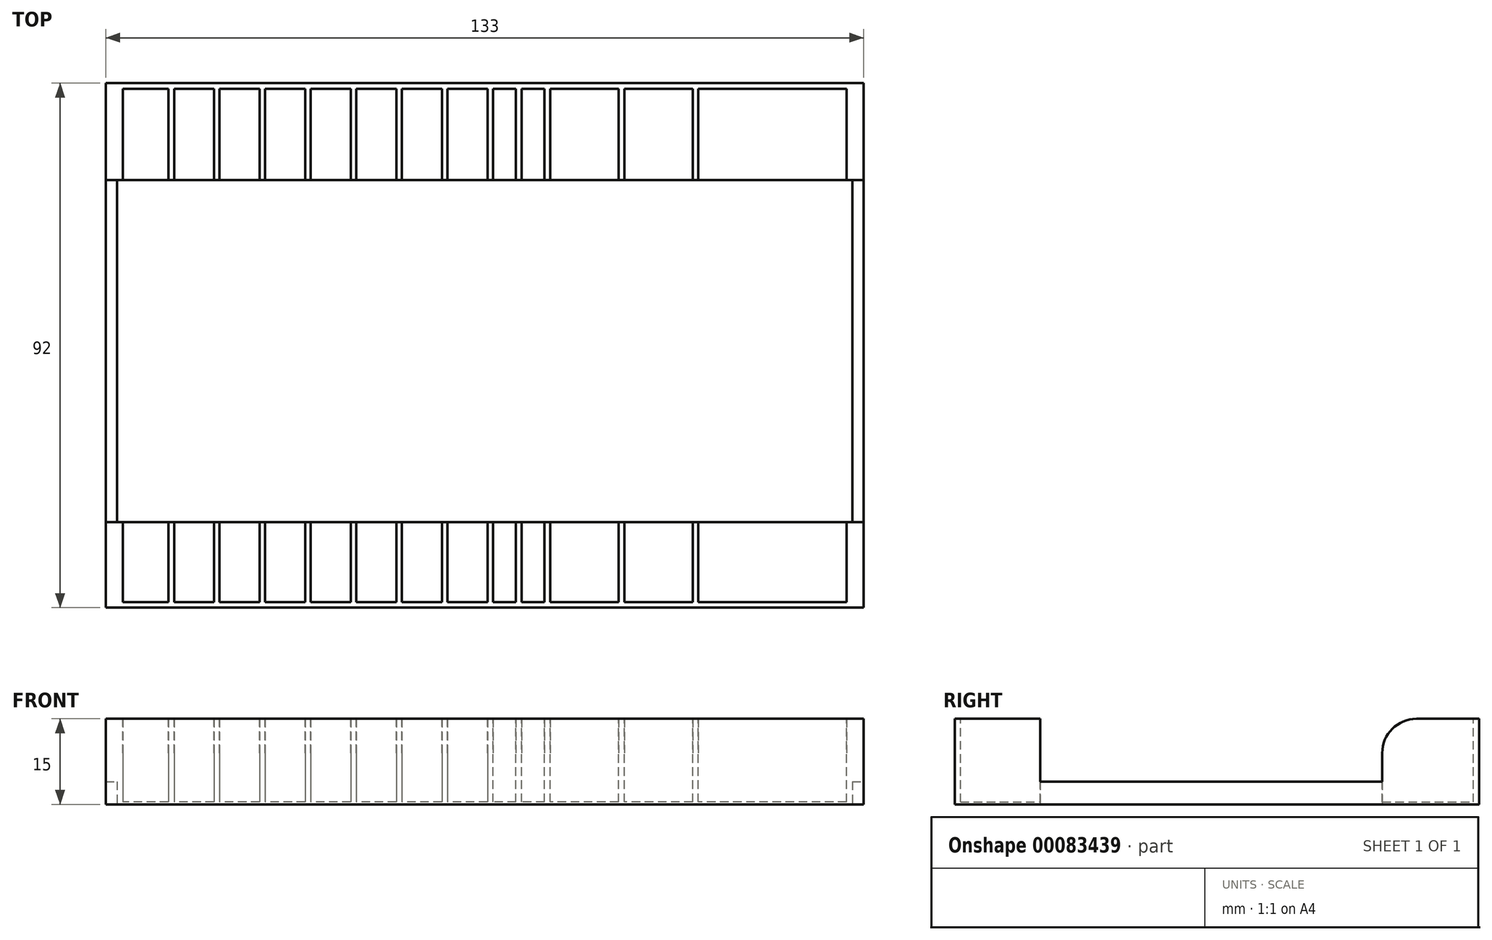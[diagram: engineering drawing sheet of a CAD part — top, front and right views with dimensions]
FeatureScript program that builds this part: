
annotation { "Feature Type Name" : "Feature", "Feature Type Description" : "" }
export const myFeature = defineFeature(function(context is Context, id is Id, definition is map)
    precondition{}
    {
        {
            assignVariable(context, id + "F0", {"name" : "holderHeight", "anyValue" : 15});
        }
        {
            var Q0;
            Q0=qCreatedBy(makeId("Top.planeOp"),FACE);
            var sketch = newSketch(context, id + "F1", { "sketchPlane" : qUnion([Q0])});
            skLineSegment(sketch, "E0.bottom", {"start": v(-58, -45) * mm, "end": v(71, -45) * mm});
            skLineSegment(sketch, "E0.top", {"start": v(-58, 47) * mm, "end": v(71, 47) * mm});
            skLineSegment(sketch, "E0.left", {"start": v(-58, -45) * mm, "end": v(-58, 47) * mm});
            skLineSegment(sketch, "E0.right", {"start": v(71, -45) * mm, "end": v(71, 47) * mm});
            skSolve(sketch);
        }
        {
            var Q0;
            Q0=makeQuery(id+"F1.imprint","IMPRINT",FACE,{"disambiguationData":[TD([[makeQuery(id+"F1.imprint","IMPRINT",EDGE,{"derivedFrom":sQuery(id+"F1.wireOp",EDGE,"E0.bottom")}),1.0]])]});
            extrude(context, id + "F2", {"entities" : qUnion([Q0]), "depth" : getVariable(context, 'holderHeight') * mm});
        }
        {
            var Q0;
            Q0=makeQuery(id+"F2.opExtrude","CAP_FACE",FACE,{"disambiguationData":[OSD([sQuery(id+"F1.wireOp",EDGE,"E0.bottom"),sQuery(id+"F1.wireOp",EDGE,"E0.top"),sQuery(id+"F1.wireOp",EDGE,"E0.left"),sQuery(id+"F1.wireOp",EDGE,"E0.right")])],"isStart":false});
            var sketch = newSketch(context, id + "F3", { "sketchPlane" : qUnion([Q0])});
            skPoint(sketch, "E1.middle", {"position": v(0, 1) * mm});
            skLineSegment(sketch, "E2.bottom", {"start": v(-49, 46) * mm, "end": v(-57, 46) * mm});
            skLineSegment(sketch, "E2.top", {"start": v(-49, -44) * mm, "end": v(-57, -44) * mm});
            skLineSegment(sketch, "E2.left", {"start": v(-49, 46) * mm, "end": v(-49, -44) * mm});
            skLineSegment(sketch, "E2.right", {"start": v(-57, 46) * mm, "end": v(-57, -44) * mm});
            skPoint(sketch, "E2.middle", {"position": v(-53, 1) * mm});
            skLineSegment(sketch, "E3", {"start": v(0, 1) * mm, "end": v(-109.38, 1) * mm, "construction": true});
            skLineSegment(sketch, "E4.bottom", {"start": v(-41, 46) * mm, "end": v(-48, 46) * mm});
            skLineSegment(sketch, "E4.top", {"start": v(-41, -44) * mm, "end": v(-48, -44) * mm});
            skLineSegment(sketch, "E4.left", {"start": v(-41, 46) * mm, "end": v(-41, -44) * mm});
            skLineSegment(sketch, "E4.right", {"start": v(-48, 46) * mm, "end": v(-48, -44) * mm});
            skPoint(sketch, "E4.middle", {"position": v(-44.5, 1) * mm});
            skPoint(sketch, "E4.cornerSnap0", {"position": v(-53, 46) * mm});
            skLineSegment(sketch, "E5.1.0.0", {"start": v(-33, 46) * mm, "end": v(-33, -44) * mm});
            skLineSegment(sketch, "E5.1.0.1", {"start": v(-33, 46) * mm, "end": v(-40, 46) * mm});
            skLineSegment(sketch, "E5.1.0.2", {"start": v(-40, 46) * mm, "end": v(-40, -44) * mm});
            skLineSegment(sketch, "E5.1.0.3", {"start": v(-33, -44) * mm, "end": v(-40, -44) * mm});
            skLineSegment(sketch, "E5.2.0.0", {"start": v(-25, 46) * mm, "end": v(-25, -44) * mm});
            skLineSegment(sketch, "E5.2.0.1", {"start": v(-25, 46) * mm, "end": v(-32, 46) * mm});
            skLineSegment(sketch, "E5.2.0.2", {"start": v(-32, 46) * mm, "end": v(-32, -44) * mm});
            skLineSegment(sketch, "E5.2.0.3", {"start": v(-25, -44) * mm, "end": v(-32, -44) * mm});
            skLineSegment(sketch, "E5.3.0.0", {"start": v(-17, 46) * mm, "end": v(-17, -44) * mm});
            skLineSegment(sketch, "E5.3.0.1", {"start": v(-17, 46) * mm, "end": v(-24, 46) * mm});
            skLineSegment(sketch, "E5.3.0.2", {"start": v(-24, 46) * mm, "end": v(-24, -44) * mm});
            skLineSegment(sketch, "E5.3.0.3", {"start": v(-17, -44) * mm, "end": v(-24, -44) * mm});
            skLineSegment(sketch, "E5.4.0.0", {"start": v(-9, 46) * mm, "end": v(-9, -44) * mm});
            skLineSegment(sketch, "E5.4.0.1", {"start": v(-9, 46) * mm, "end": v(-16, 46) * mm});
            skLineSegment(sketch, "E5.4.0.2", {"start": v(-16, 46) * mm, "end": v(-16, -44) * mm});
            skLineSegment(sketch, "E5.4.0.3", {"start": v(-9, -44) * mm, "end": v(-16, -44) * mm});
            skLineSegment(sketch, "E5.5.0.0", {"start": v(-1, 46) * mm, "end": v(-1, -44) * mm});
            skLineSegment(sketch, "E5.5.0.1", {"start": v(-1, 46) * mm, "end": v(-8, 46) * mm});
            skLineSegment(sketch, "E5.5.0.2", {"start": v(-8, 46) * mm, "end": v(-8, -44) * mm});
            skLineSegment(sketch, "E5.5.0.3", {"start": v(-1, -44) * mm, "end": v(-8, -44) * mm});
            skLineSegment(sketch, "E5.direction1", {"start": v(-41, -44) * mm, "end": v(-33, -44) * mm, "construction": true});
            skLineSegment(sketch, "E6.0.6.0", {"start": v(7, 46) * mm, "end": v(7, -44) * mm});
            skLineSegment(sketch, "E6.3.6.0", {"start": v(7, 46) * mm, "end": v(0, 46) * mm});
            skLineSegment(sketch, "E6.6.6.0", {"start": v(0, 46) * mm, "end": v(0, -44) * mm});
            skLineSegment(sketch, "E6.9.6.0", {"start": v(7, -44) * mm, "end": v(0, -44) * mm});
            skLineSegment(sketch, "E7", {"start": v(0, 1) * mm, "end": v(83.05, 1) * mm, "construction": true});
            skLineSegment(sketch, "E8.bottom", {"start": v(8, -44) * mm, "end": v(12, -44) * mm});
            skLineSegment(sketch, "E8.top", {"start": v(8, 46) * mm, "end": v(12, 46) * mm});
            skLineSegment(sketch, "E8.left", {"start": v(8, -44) * mm, "end": v(8, 46) * mm});
            skLineSegment(sketch, "E8.right", {"start": v(12, -44) * mm, "end": v(12, 46) * mm});
            skPoint(sketch, "E8.middle", {"position": v(10, 1) * mm});
            skLineSegment(sketch, "E9.bottom", {"start": v(13, -44) * mm, "end": v(17, -44) * mm});
            skLineSegment(sketch, "E9.top", {"start": v(13, 46) * mm, "end": v(17, 46) * mm});
            skLineSegment(sketch, "E9.left", {"start": v(13, -44) * mm, "end": v(13, 46) * mm});
            skLineSegment(sketch, "E9.right", {"start": v(17, -44) * mm, "end": v(17, 46) * mm});
            skPoint(sketch, "E9.middle", {"position": v(15, 1) * mm});
            skLineSegment(sketch, "E10.bottom", {"start": v(18, -44) * mm, "end": v(30, -44) * mm});
            skLineSegment(sketch, "E10.top", {"start": v(18, 46) * mm, "end": v(30, 46) * mm});
            skLineSegment(sketch, "E10.left", {"start": v(18, -44) * mm, "end": v(18, 46) * mm});
            skLineSegment(sketch, "E10.right", {"start": v(30, -44) * mm, "end": v(30, 46) * mm});
            skPoint(sketch, "E10.middle", {"position": v(24, 1) * mm});
            skLineSegment(sketch, "E11.1.0.0", {"start": v(43, -44) * mm, "end": v(43, 46) * mm});
            skLineSegment(sketch, "E11.1.0.1", {"start": v(31, 46) * mm, "end": v(43, 46) * mm});
            skLineSegment(sketch, "E11.1.0.2", {"start": v(31, -44) * mm, "end": v(31, 46) * mm});
            skLineSegment(sketch, "E11.1.0.3", {"start": v(31, -44) * mm, "end": v(43, -44) * mm});
            skLineSegment(sketch, "E11.direction1", {"start": v(30, -44) * mm, "end": v(43, -44) * mm, "construction": true});
            skLineSegment(sketch, "E12.bottom", {"start": v(44, -44) * mm, "end": v(70, -44) * mm});
            skLineSegment(sketch, "E12.top", {"start": v(44, 46) * mm, "end": v(70, 46) * mm});
            skLineSegment(sketch, "E12.left", {"start": v(44, -44) * mm, "end": v(44, 46) * mm});
            skLineSegment(sketch, "E12.right", {"start": v(70, -44) * mm, "end": v(70, 46) * mm});
            skPoint(sketch, "E12.middle", {"position": v(57, 1) * mm});
            skSolve(sketch);
        }
        {
            var Q0;
            Q0=makeQuery(id+"F2.opExtrude","CAP_FACE",FACE,{"disambiguationData":[OSD([sQuery(id+"F1.wireOp",EDGE,"E0.bottom"),sQuery(id+"F1.wireOp",EDGE,"E0.top"),sQuery(id+"F1.wireOp",EDGE,"E0.left"),sQuery(id+"F1.wireOp",EDGE,"E0.right")])],"isStart":false});
            var sketch = newSketch(context, id + "F4", { "sketchPlane" : qUnion([Q0])});
            skLineSegment(sketch, "E13.bottom", {"start": v(-58, -30) * mm, "end": v(71, -30) * mm});
            skLineSegment(sketch, "E13.top", {"start": v(-58, 30) * mm, "end": v(71, 30) * mm});
            skLineSegment(sketch, "E13.left", {"start": v(-58, -30) * mm, "end": v(-58, 30) * mm});
            skLineSegment(sketch, "E13.right", {"start": v(71, -30) * mm, "end": v(71, 30) * mm});
            skPoint(sketch, "E13.middle", {"position": v(6.5, 0) * mm});
            skLineSegment(sketch, "E14", {"start": v(-73, 0) * mm, "end": v(86, 0) * mm, "construction": true});
            skSolve(sketch);
        }
        {
            var Q0;
            Q0 = qSketchRegion(id + "F4", true);
            extrude(context, id + "F5", {"entities" : qUnion([Q0]), "operationType" : NewBodyOperationType.REMOVE, "oppositeDirection" : true, "depth" : (getVariable(context, 'holderHeight') - 4) * mm});
        }
        {
            var Q0;
            Q0=makeQuery(id+"F5.boolean.opBoolean","COPY",EDGE,{"derivedFrom":makeQuery(id+"F5.opExtrude","CAP_EDGE",EDGE,{"disambiguationData":[OSD([sQuery(id+"F4.wireOp",EDGE,"E13.top")])],"isStart":true})});
            var Q1;
            Q1=makeQuery(id+"F5.boolean.opBoolean","COPY",EDGE,{"derivedFrom":makeQuery(id+"F5.opExtrude","CAP_EDGE",EDGE,{"disambiguationData":[OSD([sQuery(id+"F4.wireOp",EDGE,"E13.bottom")])],"isStart":true})});
            fillet(context, id + "F6", {"entities" : qUnion([Q0, Q1]), "radius" : 6 * mm, "tangentPropagation" : true, "allowEdgeOverflow" : false});
        }
        {
            var Q0;
            Q0=makeQuery(id+"F3.imprint","IMPRINT",FACE,{"disambiguationData":[TD([[makeQuery(id+"F3.imprint","IMPRINT",EDGE,{"derivedFrom":sQuery(id+"F3.wireOp",EDGE,"E2.bottom")}),1.0]])]});
            var Q1;
            Q1=makeQuery(id+"F3.imprint","IMPRINT",FACE,{"disambiguationData":[TD([[makeQuery(id+"F3.imprint","IMPRINT",EDGE,{"derivedFrom":sQuery(id+"F3.wireOp",EDGE,"E4.bottom")}),1.0]])]});
            var Q2;
            Q2=makeQuery(id+"F3.imprint","IMPRINT",FACE,{"disambiguationData":[TD([[makeQuery(id+"F3.imprint","IMPRINT",EDGE,{"derivedFrom":sQuery(id+"F3.wireOp",EDGE,"E5.1.0.0")}),-1.0]])]});
            var Q3;
            Q3=makeQuery(id+"F3.imprint","IMPRINT",FACE,{"disambiguationData":[TD([[makeQuery(id+"F3.imprint","IMPRINT",EDGE,{"derivedFrom":sQuery(id+"F3.wireOp",EDGE,"E5.2.0.0")}),-1.0]])]});
            var Q4;
            Q4=makeQuery(id+"F3.imprint","IMPRINT",FACE,{"disambiguationData":[TD([[makeQuery(id+"F3.imprint","IMPRINT",EDGE,{"derivedFrom":sQuery(id+"F3.wireOp",EDGE,"E5.3.0.0")}),-1.0]])]});
            var Q5;
            Q5=makeQuery(id+"F3.imprint","IMPRINT",FACE,{"disambiguationData":[TD([[makeQuery(id+"F3.imprint","IMPRINT",EDGE,{"derivedFrom":sQuery(id+"F3.wireOp",EDGE,"E5.4.0.0")}),-1.0]])]});
            var Q6;
            Q6=makeQuery(id+"F3.imprint","IMPRINT",FACE,{"disambiguationData":[TD([[makeQuery(id+"F3.imprint","IMPRINT",EDGE,{"derivedFrom":sQuery(id+"F3.wireOp",EDGE,"E5.5.0.0")}),-1.0]])]});
            var Q7;
            Q7=makeQuery(id+"F3.imprint","IMPRINT",FACE,{"disambiguationData":[TD([[makeQuery(id+"F3.imprint","IMPRINT",EDGE,{"derivedFrom":sQuery(id+"F3.wireOp",EDGE,"E6.0.6.0")}),-1.0]])]});
            var Q8;
            Q8=makeQuery(id+"F3.imprint","IMPRINT",FACE,{"disambiguationData":[TD([[makeQuery(id+"F3.imprint","IMPRINT",EDGE,{"derivedFrom":sQuery(id+"F3.wireOp",EDGE,"E8.bottom")}),1.0]])]});
            var Q9;
            Q9=makeQuery(id+"F3.imprint","IMPRINT",FACE,{"disambiguationData":[TD([[makeQuery(id+"F3.imprint","IMPRINT",EDGE,{"derivedFrom":sQuery(id+"F3.wireOp",EDGE,"E9.bottom")}),1.0]])]});
            var Q10;
            Q10=makeQuery(id+"F3.imprint","IMPRINT",FACE,{"disambiguationData":[TD([[makeQuery(id+"F3.imprint","IMPRINT",EDGE,{"derivedFrom":sQuery(id+"F3.wireOp",EDGE,"E10.bottom")}),1.0]])]});
            var Q11;
            Q11=makeQuery(id+"F3.imprint","IMPRINT",FACE,{"disambiguationData":[TD([[makeQuery(id+"F3.imprint","IMPRINT",EDGE,{"derivedFrom":sQuery(id+"F3.wireOp",EDGE,"E11.1.0.0")}),1.0]])]});
            var Q12;
            Q12=makeQuery(id+"F3.imprint","IMPRINT",FACE,{"disambiguationData":[TD([[makeQuery(id+"F3.imprint","IMPRINT",EDGE,{"derivedFrom":sQuery(id+"F3.wireOp",EDGE,"E12.bottom")}),1.0]])]});
            extrude(context, id + "F7", {"entities" : qUnion([Q0, Q1, Q2, Q3, Q4, Q5, Q6, Q7, Q8, Q9, Q10, Q11, Q12]), "operationType" : NewBodyOperationType.REMOVE, "oppositeDirection" : true, "depth" : (getVariable(context, 'holderHeight') - .4) * mm});
        }
        {
            var Q0;
            Q0=makeQuery(id+"F2.opExtrude","SWEPT_FACE",FACE,{"disambiguationData":[OSD([sQuery(id+"F1.wireOp",EDGE,"E0.left")])]});
            extrude(context, id + "F8", {"entities" : qUnion([Q0]), "operationType" : NewBodyOperationType.ADD, "depth" : 2 * mm});
        }
        {
            var Q0;
            Q0=makeQuery(id+"F2.opExtrude","SWEPT_FACE",FACE,{"disambiguationData":[OSD([sQuery(id+"F1.wireOp",EDGE,"E0.right")])]});
            extrude(context, id + "F9", {"entities" : qUnion([Q0]), "operationType" : NewBodyOperationType.ADD, "depth" : 2 * mm});
        }
        {
            var Q0;
            {var subQ0=sQuery(id+"F1.wireOp",EDGE,"E0.right");var subQ1=sQuery(id+"F1.wireOp",EDGE,"E0.left");Q0=makeQuery(id+"F9.boolean.opBoolean","MERGE",FACE,{"derivedFrom":[makeQuery(id+"F8.boolean.opBoolean","MERGE",FACE,{"derivedFrom":[makeQuery(id+"F2.opExtrude","CAP_FACE",FACE,{"disambiguationData":[OSD([sQuery(id+"F1.wireOp",EDGE,"E0.bottom"),sQuery(id+"F1.wireOp",EDGE,"E0.top"),subQ1,subQ0])],"isStart":true}),makeQuery(id+"F8.opExtrude","SWEPT_FACE",FACE,{"disambiguationData":[OSD([subQ1]),TDD([makeQuery(id+"F2.opExtrude","CAP_EDGE",EDGE,{"disambiguationData":[OSD([subQ1])],"isStart":true})])]})]}),makeQuery(id+"F9.opExtrude","SWEPT_FACE",FACE,{"disambiguationData":[OSD([subQ0]),TDD([makeQuery(id+"F2.opExtrude","CAP_EDGE",EDGE,{"disambiguationData":[OSD([subQ0])],"isStart":true})])]})]});}
            var sketch = newSketch(context, id + "F10", { "sketchPlane" : qUnion([Q0])});
            skLineSegment(sketch, "E15", {"start": v(6.5, 45) * mm, "end": v(6.5, -47) * mm, "construction": true});
            skLineSegment(sketch, "E16", {"start": v(73, -1) * mm, "end": v(-60, -1) * mm, "construction": true});
            skLineSegment(sketch, "E17.bottom", {"start": v(-58, -30) * mm, "end": v(71, -30) * mm});
            skLineSegment(sketch, "E17.top", {"start": v(-58, 30) * mm, "end": v(71, 30) * mm});
            skLineSegment(sketch, "E17.left", {"start": v(-58, -30) * mm, "end": v(-58, 30) * mm});
            skLineSegment(sketch, "E17.right", {"start": v(71, -30) * mm, "end": v(71, 30) * mm});
            skPoint(sketch, "E17.middle", {"position": v(6.5, 0) * mm});
            skPoint(sketch, "E17.middle.positionSnap0", {"position": v(6.5, -1) * mm});
            skPoint(sketch, "E17.centerSnap0", {"position": v(6.5, -1) * mm});
            skSolve(sketch);
        }
        {
            var Q0;
            Q0=makeQuery(id+"F10.imprint","IMPRINT",FACE,{"disambiguationData":[TD([[makeQuery(id+"F10.imprint","IMPRINT",EDGE,{"derivedFrom":sQuery(id+"F10.wireOp",EDGE,"E17.bottom")}),1.0]])]});
            extrude(context, id + "F11", {"entities" : qUnion([Q0]), "operationType" : NewBodyOperationType.REMOVE, "oppositeDirection" : true, "depth" : 25 * mm});
        }
    });
